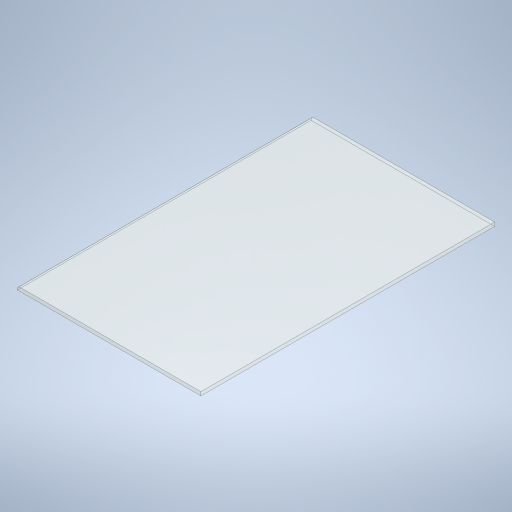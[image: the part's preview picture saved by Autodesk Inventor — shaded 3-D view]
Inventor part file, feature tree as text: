
AUTODESK INVENTOR PART (.ipt)
format: ipt  version: 2023 (Build 270158000, 158)  size: 290,304 bytes
history: native  units: in
note: dims shown in document units (in); Inventor stores cm internally (conversion verified against a paired STEP export)
features: extrude x1, chamfer x1, sketch x1
ambient origin geometry x8: Origin, YZ Plane, XZ Plane, XY Plane, X Axis, Y Axis, Z Axis, Center Point
bodies: Solid1 (feature_tree)
feature tree (3):
  extrude  "Extrusion1"  Depth=0.2in
  chamfer  "Chamfer1"  Distance=1.0in
  sketch  "Sketch1"  dims[d0=54.0in d1=54.0in d2=1.0in d3=1.0in d4=8.0in d5=16.0in d6=8.0in d7=16.0in d8=16.0in d9=8.0in d10=16.0in d11=8.0in d12=4.0in d13=4.0in d14=4.0in d15=4.0in d16=17.0in d17=17.0in d18=17.0in d19=17.0in d20=20.0in d21=1.0in d22=1.0in d23=1.0in d24=1.0in d25=45.0deg d26=2.5in d27=45.0deg d28=45.0deg d29=45.0deg d30=1.0in d31=1.0in d32=1.0in d33=1.0in d34=0.25in d35=0.25in d36=0.25in d37=0.25in d38=0.25in d39=0.25in d40=0.25in d41=0.25in d42=0.2in d43=0.0in d44=0.1in d45=0.125in d46=45.0deg]
